# Revit family: Sanitary_Showers_AXOR_12427XXX-AXOR-ShowerSolutions-ShowerHeav___
name_source: partatom
category: Plumbing Fixtures
units: mm (PartAtom-declared; Revit-internal decimal feet)

## family parameters
Always vertical = No
Cut with Voids When Loaded = No
OmniClass Number = 23.31.17.00
OmniClass Title = Showers
Part Type = Normal
Room Calculation Point = No
Round Connector Dimension = Use Diameter
Shared = No
Work Plane-Based = Yes

## types (1)
- Default - please load Revit Family Type Catalog
    Assembly Code = D2010 | Plumbing Fixtures
    Default Elevation = 1219.2 mm  [stored 4 ft]
    Description = AXOR ShowerSolutions ShowerHeaven 1200/300 4jet with light module 3500 K
    ETIM Code = EC011383
    ETIM Title = Shower head
    GTIN code = 4059625524985
    Keynote = 22 41 23 | Residential Showers
    Manufacturer = AXOR
    Material 1 = AXOR - Metal - 000 Chrome
    Model = 12427XXX
    Product data url = https://bimobject.com
    Product url = https://www.axor-design.com
    URL = https://www.axor-design.com
    Uniclass 2015 Code = EC011383
    Uniclass 2015 Name = Shower head
    Version = 1

note: [stored X ft] marks values corroborated as IEEE doubles in the binary element streams (Revit-internal decimal feet)

## geometry (parser evidence)
native form markers: Sweep x2
no freeform markers — native parametric forms only
